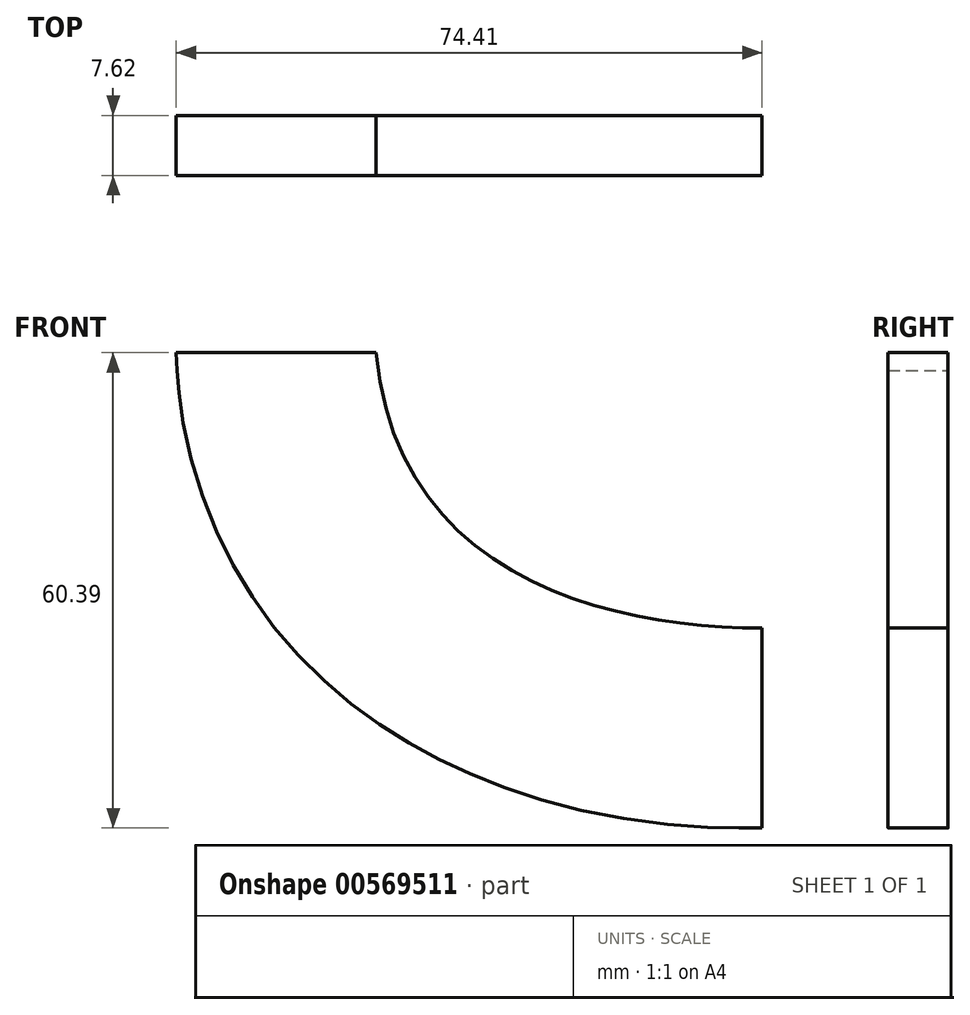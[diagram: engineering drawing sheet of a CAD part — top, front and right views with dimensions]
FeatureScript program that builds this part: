
annotation { "Feature Type Name" : "Feature", "Feature Type Description" : "" }
export const myFeature = defineFeature(function(context is Context, id is Id, definition is map)
    precondition{}
    {
        {
            var Q0;
            Q0=qCreatedBy(makeId("Front.planeOp"),FACE);
            var sketch = newSketch(context, id + "F0", { "sketchPlane" : qUnion([Q0])});
            skLineSegment(sketch, "E0", {"start": v(40.33, -14.88) * mm, "end": v(40.33, -40.28) * mm});
            skFitSpline(sketch, "E1", {"points": [v(40.33, -14.88) * mm, v(-8.68, 20.1) * mm], "startDerivative": vector(-56.3, 0) * mm, "endDerivative": vector(-7.93, 87.04) * mm});
            skFitSpline(sketch, "E2.0", {"points": [v(40.33, -40.28) * mm, v(37.3, -40.28) * mm, v(30.91, -40.04) * mm, v(20.44, -38.67) * mm, v(11.16, -36.35) * mm, v(3.55, -33.5) * mm, v(-2.2, -30.78) * mm, v(-7.92, -27.37) * mm, v(-13.47, -23.2) * mm, v(-18.72, -18.18) * mm, v(-23.46, -12.3) * mm, v(-27.5, -5.65) * mm, v(-30.68, 1.69) * mm, v(-32.9, 9.54) * mm, v(-33.72, 15.02) * mm, v(-33.98, 17.8) * mm]});
            skLineSegment(sketch, "E3", {"start": v(-8.68, 20.1) * mm, "end": v(-34.08, 20.1) * mm});
            skLineSegment(sketch, "E4", {"start": v(-34.08, 20.1) * mm, "end": v(-33.98, 17.8) * mm});
            skLineSegment(sketch, "E5.bottom", {"start": v(-34.08, 20.1) * mm, "end": v(-8.68, 20.1) * mm});
            skLineSegment(sketch, "E5.top", {"start": v(-34.08, 96.3) * mm, "end": v(-8.68, 96.3) * mm});
            skLineSegment(sketch, "E5.left", {"start": v(-34.08, 20.1) * mm, "end": v(-34.08, 96.3) * mm});
            skLineSegment(sketch, "E5.right", {"start": v(-8.68, 20.1) * mm, "end": v(-8.68, 96.3) * mm});
            skSolve(sketch);
        }
        {
            var Q0;
            Q0=makeQuery(id+"F0.imprint","IMPRINT",FACE,{"disambiguationData":[TD([[makeQuery(id+"F0.imprint","IMPRINT",EDGE,{"derivedFrom":sQuery(id+"F0.wireOp",EDGE,"E0")}),-1.0]])]});
            var Q1;
            Q1=makeQuery(id+"F0.imprint","IMPRINT",FACE,{"disambiguationData":[TD([[makeQuery(id+"F0.imprint","IMPRINT",EDGE,{"derivedFrom":sQuery(id+"F0.wireOp",EDGE,"E5.bottom")}),1.0]])]});
            extrude(context, id + "F1", {"entities" : qUnion([Q0, Q1]), "depth" : 7.62 * mm, "offsetDistance" : 25.4 * mm});
        }
        {
            var Q0;
            Q0=makeQuery(id+"F1.opExtrude","CAP_FACE",FACE,{"disambiguationData":[OSD([sQuery(id+"F0.wireOp",EDGE,"E0"),sQuery(id+"F0.wireOp",EDGE,"E1"),sQuery(id+"F0.wireOp",EDGE,"E2.0"),sQuery(id+"F0.wireOp",EDGE,"E4"),sQuery(id+"F0.wireOp",EDGE,"E5.top"),sQuery(id+"F0.wireOp",EDGE,"E5.left"),sQuery(id+"F0.wireOp",EDGE,"E5.right")])],"isStart":false});
            var sketch = newSketch(context, id + "F2", { "sketchPlane" : qUnion([Q0])});
            skPoint(sketch, "E6", {"position": v(-21.38, 45.5) * mm});
            skSolve(sketch);
        }
        {
            var Q0;
            Q0=sQuery(id+"F2.wireOp",VERTEX,"E6");
            var Q1;
            Q1=makeQuery(id+"F1.opExtrude","SWEPT_BODY",BODY,{"disambiguationData":[OSD([sQuery(id+"F0.wireOp",EDGE,"E0"),sQuery(id+"F0.wireOp",EDGE,"E1"),sQuery(id+"F0.wireOp",EDGE,"E2.0"),sQuery(id+"F0.wireOp",EDGE,"E4"),sQuery(id+"F0.wireOp",EDGE,"E5.top"),sQuery(id+"F0.wireOp",EDGE,"E5.left"),sQuery(id+"F0.wireOp",EDGE,"E5.right")])]});
            hole(context, id + "F3", {"style" : HoleStyle.SIMPLE, "endStyle" : HoleEndStyle.THROUGH, "holeDiameter" : 5.08 * mm, "isTappedThrough" : true, "tappedDepth" : 12.7 * mm, "tapClearance" : 3, "locations" : qUnion([Q0]), "scope" : qUnion([Q1])});
        }
    });
